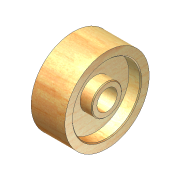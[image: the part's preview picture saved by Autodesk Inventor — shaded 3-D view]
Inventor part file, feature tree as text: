
AUTODESK INVENTOR PART (.ipt)
format: ipt  version: unknown  size: 206,336 bytes
history: native  units: in
note: dims shown in document units (in); Inventor stores cm internally (conversion verified against a paired STEP export)
features: revolve x1, chamfer x1, sketch x1
ambient origin geometry x8: Origin, YZ Plane, XZ Plane, XY Plane, X Axis, Y Axis, Z Axis, Center Point
feature tree (3):
  revolve  "Revolution1"  [1 undecoded]
  chamfer  "Chamfer1"  Angle=90.0deg  [1 undecoded]
  sketch  "Sketch1"  dims[d0=0.9843in d2=0.2756in d4=0.2362in d5=90.0deg d14=0.1181in d19=0.0197in d20=0.0787in d21=45.0deg d24=0.1969in d25=0.1181in d30=0.3937in d31=0.7874in d35=0.3937in]
note: 2 required parameter values undecoded (feature->parameter linkage not recoverable at this tier; creation-order binding heuristic only, values carry confidence <= 0.55)